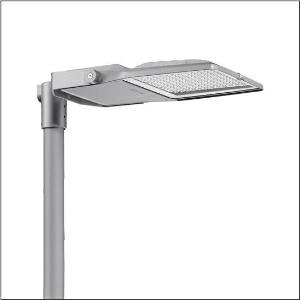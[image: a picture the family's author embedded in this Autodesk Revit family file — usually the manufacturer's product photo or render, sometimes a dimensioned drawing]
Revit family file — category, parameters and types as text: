
# Revit family: floodlight_fl_21_iq_midi___pl43_5xa7782f4a3a_c232
name_source: partatom
category: Lighting Fixtures
units: mm (PartAtom-declared; Revit-internal decimal feet)

## family parameters
Cut with Voids When Loaded = No
Host = Face
Light Source = No
Part Type = Normal
Room Calculation Point = No
Round Connector Dimension = Use Diameter
Shared = No

## types (1)
- --- (1 x LED, 38290 lm, 270.2 W, 4000K)
    Apparent Load = 270 VA
    CIE Flux Codes = 27 78 99 100 100
    Color Rendering = 70
    Color Temperature = 4000K
    Default Elevation = 1800 mm
    Description = Floodlight FL 21 iQ midi, floodlight, primary light control with lens, of PMMA, primary optical cover: protective disc, of toughened safety glass, transparent, light distribution: PL43, light emission: direct distribution, installation type: surface-mounted, LED, High Power LED, rated luminous flux: 38.290lm, luminous efficacy: 142lm/W, light colour: 740, colour temperature: 4000K, control gear: ECG iQ, control: optimised constant luminous flux control (CLO 2.0), Desk-Remote (wireless, voltage-free reading and setting of iQ features in the workshop via application-optimized NFC function/RFID function), Smart-Wire, Night-Set, Temp-Guard, Auto-Match, Street-Remote, with terminal, 6-pole, mains connection: 220..240V, AC, 50/60Hz, start of lifetime: 270W, end of service life: 287W, reduction: 118W, luminaire housing, of diecast aluminium, powder-coated, Siteco® metallic grey (DB 702S), corrosivity category C5 mid according to DIN EN ISO 12944, sealing non-destructively replaceable, please order mast flange separately, mast bracket, of steel, galvanised, powder-coated, Siteco® metallic grey (DB 702S), protection rating (complete): IP66, insulation class (complete): insulation class II (safety insulation), certification: CE, ENEC, VDE, protection symbol: D, impact resistance: IK08, permissible operating ambient temperature: -40..+40°C, permissible operating ambient temperature for outdoor applications: -40..+50°C, standard: DIN EN 12944, LABS conformity tested according to VDMA 24364:2018-05, packaging unit: 1 piece

Light Distribution: PL43
    Height = 76 mm
    Lamp = 1 x LED
    Lamp Light Flux = 38290 lm
    Lamp Power = 270.2 W
    Lamp count = 1
    Length = 657 mm
    Luminous efficacy = 142 lm/W
    Manufacturer = Siteco
    ModVariant = No
    Model = 5XA7782F4A3A
    Number of Poles = 1
    OnlyDefault = Yes
    Power Factor = 1
    Product Name = Floodlight FL 21 iQ midi | PL43
    Product group = floodlight | pylon annexe
    ProductGroupID = 6200
    Protection Class = Protection class II
    Protection Degree = IP 66
    RLX_Detail_Level = 1
    RLX_Emergency_Light_Flux = 0 lm
    RLX_Emergency_Type = 0
    RLX_Emergency_Type_DB = No
    RlxData = <blob elided: 153701 chars, md5=ff05c726>
    Socket = socket
    Standby Power = 0 W
    System Light Flux = 38290 lm
    System Power = 270 W
    Type Comments = factory setting: luminous flux: 100 % | dim-lin: 254 | 620 mA
    Type Image = l_1007123.jpg
    URL = http://relux.com
    VarID = @adj_073431
    Voltage = 0 V
    Weight = 0.00 kg
    Width = 442 mm

## geometry (parser evidence)
native form markers: Blend x4, Sweep x11
no freeform markers — native parametric forms only
